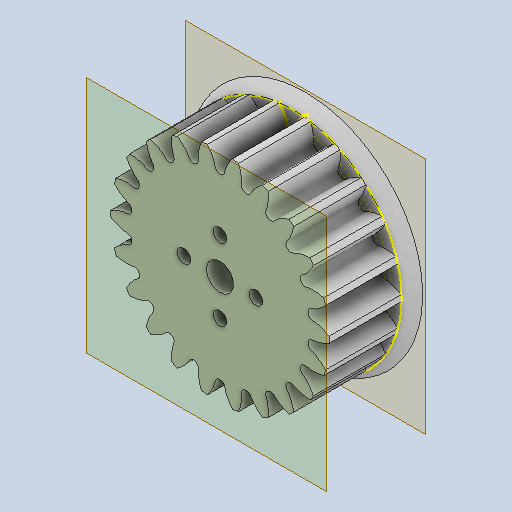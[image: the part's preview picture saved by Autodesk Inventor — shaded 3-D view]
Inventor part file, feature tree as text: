
AUTODESK INVENTOR PART (.ipt)
format: ipt  version: 2024.2 (Build 282272000, 272)  size: 423,424 bytes
history: native  units: mm
features: other x6, sketch x6
ambient origin geometry x8: Origin, YZ Plane, XZ Plane, XY Plane, X Axis, Y Axis, Z Axis, Center Point
bodies: Body1 (feature_tree)
feature tree (12):
  other  "Шест.ipt"
  other  "Твердое тело1::Шест.ipt"
  other  "Элемент создания тегов1"
  sketch  "Sketch1"  dims[d0=10.0mm]
  sketch  "Эскиз2"
  sketch  "Эскиз3"
  sketch  "Эскиз4"
  sketch  "Эскиз5"
  sketch  "Эскиз6"
  other  "РабПлоскость1"
  other  "РабПлоскость2"
  other  "Твердое тело1"
